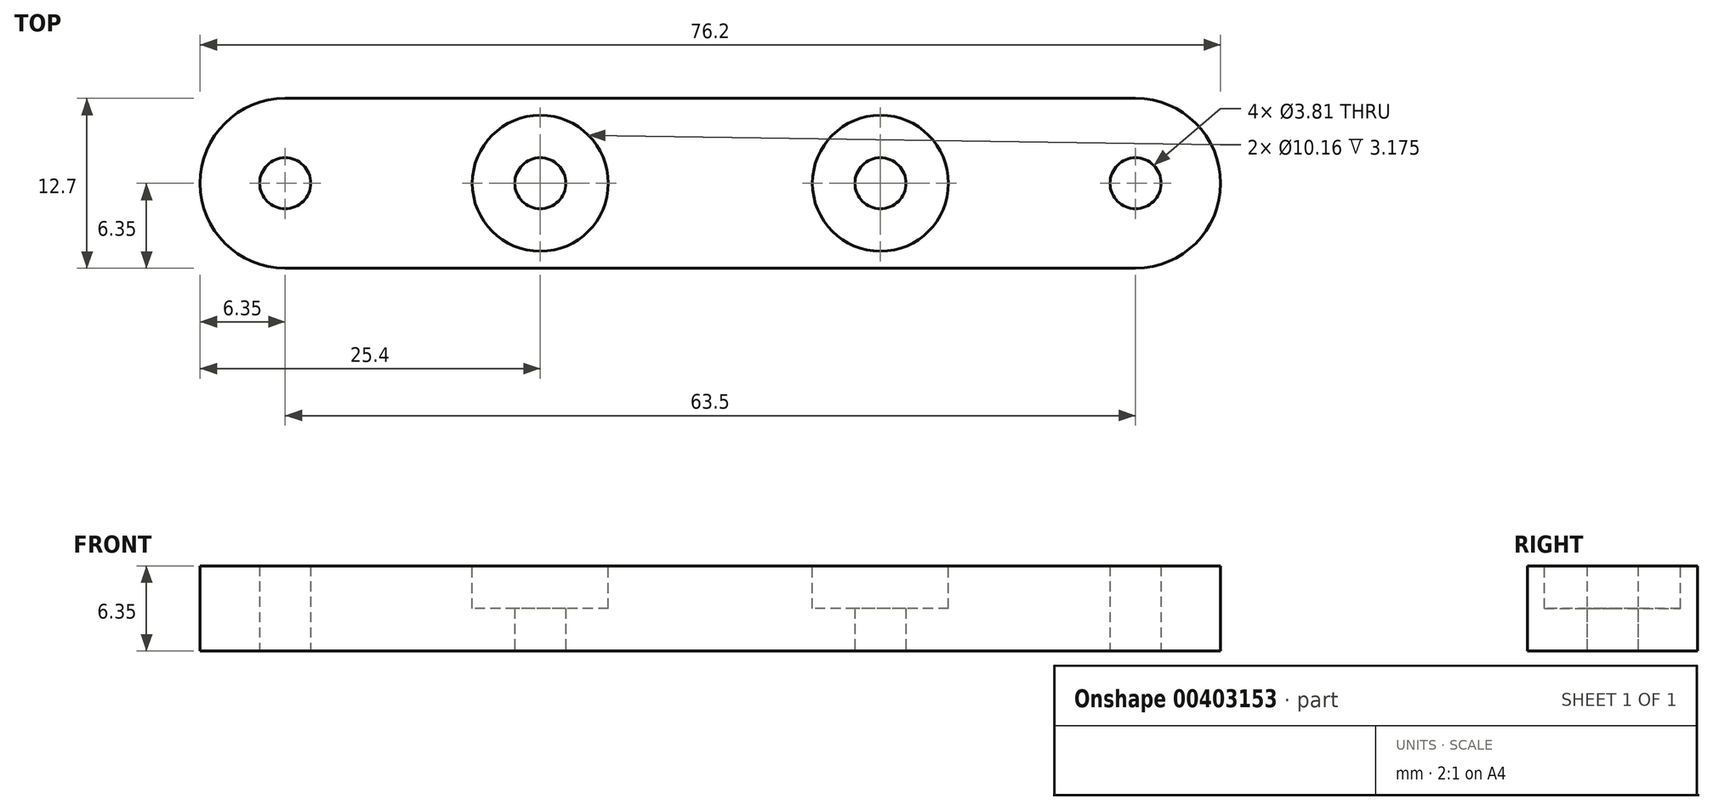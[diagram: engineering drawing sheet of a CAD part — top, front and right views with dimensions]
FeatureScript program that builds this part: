
annotation { "Feature Type Name" : "Feature", "Feature Type Description" : "" }
export const myFeature = defineFeature(function(context is Context, id is Id, definition is map)
    precondition{}
    {
        {
            var Q0;
            Q0=qCreatedBy(makeId("Top.planeOp"),FACE);
            var sketch = newSketch(context, id + "F0", { "sketchPlane" : qUnion([Q0])});
            skLineSegment(sketch, "E0.bottom", {"start": v(31.75, -6.35) * mm, "end": v(-31.75, -6.35) * mm});
            skLineSegment(sketch, "E0.top", {"start": v(31.75, 6.35) * mm, "end": v(-31.75, 6.35) * mm});
            skLineSegment(sketch, "E0.left", {"start": v(38.1, 0) * mm, "end": v(38.1, 0) * mm});
            skLineSegment(sketch, "E0.right", {"start": v(-38.1, 0) * mm, "end": v(-38.1, 0) * mm});
            skPoint(sketch, "E0.middle", {"position": v(0, 0) * mm});
            skPoint(sketch, "E1.visualSharp", {"position": v(-38.1, 6.35) * mm});
            skArc(sketch, "E1.filletArc", {"start": v(-31.75, 6.35) * mm, "mid": v(-36.24, 4.5) * mm, "end": v(-38.1, 0) * mm});
            skPoint(sketch, "E2.visualSharp", {"position": v(-38.1, -6.35) * mm});
            skArc(sketch, "E2.filletArc", {"start": v(-38.1, 0) * mm, "mid": v(-36.24, -4.5) * mm, "end": v(-31.75, -6.35) * mm});
            skPoint(sketch, "E3.visualSharp", {"position": v(38.1, -6.35) * mm});
            skArc(sketch, "E3.filletArc", {"start": v(31.75, -6.35) * mm, "mid": v(36.24, -4.5) * mm, "end": v(38.1, 0) * mm});
            skPoint(sketch, "E4.visualSharp", {"position": v(38.1, 6.35) * mm});
            skArc(sketch, "E4.filletArc", {"start": v(38.1, 0) * mm, "mid": v(36.24, 4.5) * mm, "end": v(31.75, 6.35) * mm});
            skCircle(sketch, "E5", {"center": v(-12.7, 0) * mm, "radius": 1.9 * mm});
            skCircle(sketch, "E6", {"center": v(12.7, 0) * mm, "radius": 1.9 * mm});
            skCircle(sketch, "E7", {"center": v(-31.75, 0) * mm, "radius": 1.9 * mm});
            skCircle(sketch, "E8", {"center": v(31.75, 0) * mm, "radius": 1.9 * mm});
            skSolve(sketch);
        }
        {
            var Q0;
            Q0=makeQuery(id+"F0.imprint","IMPRINT",FACE,{"disambiguationData":[TD([[makeQuery(id+"F0.imprint","IMPRINT",EDGE,{"derivedFrom":sQuery(id+"F0.wireOp",EDGE,"E0.bottom")}),-1.0]])]});
            extrude(context, id + "F1", {"entities" : qUnion([Q0]), "depth" : 6.35 * mm});
        }
        {
            var Q0;
            Q0=makeQuery(id+"F1.opExtrude","CAP_FACE",FACE,{"disambiguationData":[OSD([sQuery(id+"F0.wireOp",EDGE,"E0.bottom"),sQuery(id+"F0.wireOp",EDGE,"E0.top"),sQuery(id+"F0.wireOp",EDGE,"E1.filletArc"),sQuery(id+"F0.wireOp",EDGE,"E2.filletArc"),sQuery(id+"F0.wireOp",EDGE,"E3.filletArc"),sQuery(id+"F0.wireOp",EDGE,"E4.filletArc"),sQuery(id+"F0.wireOp",EDGE,"E5"),sQuery(id+"F0.wireOp",EDGE,"E6"),sQuery(id+"F0.wireOp",EDGE,"E7"),sQuery(id+"F0.wireOp",EDGE,"E8")])],"isStart":false});
            var sketch = newSketch(context, id + "F2", { "sketchPlane" : qUnion([Q0])});
            skCircle(sketch, "E9", {"center": v(12.7, 0) * mm, "radius": 5.08 * mm});
            skCircle(sketch, "E10", {"center": v(-12.7, 0) * mm, "radius": 5.08 * mm});
            skSolve(sketch);
        }
        {
            var Q0;
            Q0=makeQuery(id+"F2.imprint","IMPRINT",FACE,{"disambiguationData":[TD([[makeQuery(id+"F2.imprint","IMPRINT",EDGE,{"derivedFrom":sQuery(id+"F2.wireOp",EDGE,"E9")}),1.0]])]});
            var Q1;
            Q1=makeQuery(id+"F2.imprint","IMPRINT",FACE,{"disambiguationData":[TD([[makeQuery(id+"F2.imprint","IMPRINT",EDGE,{"derivedFrom":sQuery(id+"F2.wireOp",EDGE,"E10")}),1.0]])]});
            extrude(context, id + "F3", {"entities" : qUnion([Q0, Q1]), "operationType" : NewBodyOperationType.REMOVE, "oppositeDirection" : true, "depth" : 3.17 * mm});
        }
    });
